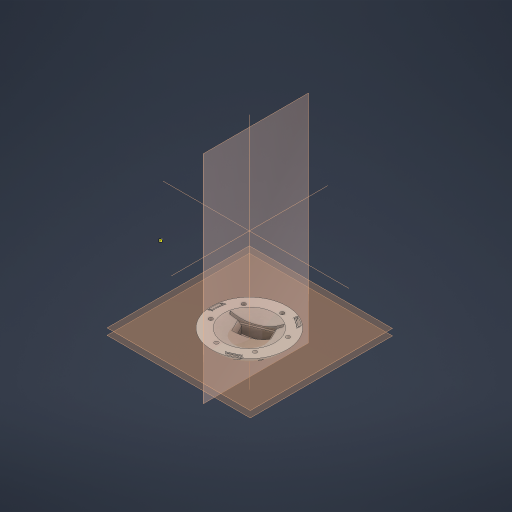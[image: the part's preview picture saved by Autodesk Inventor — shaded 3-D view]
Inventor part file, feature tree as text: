
AUTODESK INVENTOR PART (.ipt)
format: ipt  version: 2023 (Build 270158000, 158)  size: 2,185,728 bytes
history: native  units: mm
features: sketch x16, extrude x10, projected_geometry x7, other x6, plane x5, pattern_circular x4, reference x3, revolve x2, chamfer x2, sweep x1, shell x1
ambient origin geometry x8: Origin, YZ Plane, XZ Plane, XY Plane, X Axis, Y Axis, Z Axis, Center Point
bodies: Solid1 (feature_tree)
feature tree (57):
  revolve  "Revolution1"  [1 undecoded]
  sketch  "3D Sketch1"
  plane  "Work Plane1"
  sweep  "Sweep1"
  pattern_circular  "Circular Pattern1"  Count=3 Angle=360.0deg
  extrude  "Extrusion1"  TaperAngle=0.0deg  [1 undecoded]
  plane  "Work Plane3"
  sketch  "Sketch12"  dims[d16=0.2mm]
  plane  "Work Plane6"
  extrude  "Extrusion6"  Depth=10.0mm
  chamfer  "Chamfer2"  Distance=10.0mm
  pattern_circular  "Circular Pattern4"  [2 undecoded]
  shell  "Shell2"  Thickness=30.0mm
  extrude  "Extrusion8"  Depth=100.0mm
  extrude  "Extrusion2"  Depth=6.0mm
  sketch  "Sketch7"  dims[d13=1.6mm]
  plane  "Work Plane4"
  extrude  "Extrusion3"  Depth=4.0mm TaperAngle=0.0deg
  extrude  "Extrusion4"  Depth=3.5mm TaperAngle=45.0deg
  pattern_circular  "Circular Pattern2"  Count=3 Angle=360.0deg
  extrude  "Extrusion7"  TaperAngle=30.0deg  [1 undecoded]
  pattern_circular  "Circular Pattern5"  [2 undecoded]
  revolve  "Revolution2"  [1 undecoded]
  extrude  "Extrusion9"  Depth=60.0mm TaperAngle=360.0deg
  extrude  "Extrusion12"  TaperAngle=360.0deg  [1 undecoded]
  extrude  "Extrusion13"  Depth=130.0mm
  chamfer  "Chamfer3"  [1 undecoded]
  sketch  "Sketch1"  dims[d0=160.0mm d1=100.0mm]
  other  "Helical Curve2"
  other  "Project to Surface1"
  sketch  "Sketch2"  dims[d2=90.0deg d7=1200.0mm d8=637.649mm d9=252.623mm d10=0.0mm]
  sketch  "Sketch3"  dims[d11=15.0mm]
  plane  "Work Plane2"
  sketch  "Sketch6"  dims[d12=3.0mm]
  sketch  "Sketch8"  dims[d14=1.478932mm]
  sketch  "Sketch9"  dims[d15=0.2mm]
  sketch  "Sketch13"  dims[d17=0.2mm]
  sketch  "Sketch14"  dims[d18=0.0mm d19=0.0mm d20=30.0mm d21=360.0deg]
  reference  "Reference1"
  sketch  "Sketch15"  dims[d23=120.0mm d24=0.0mm d25=0.0mm]
  sketch  "Sketch16"  dims[d26=-130.0mm d27=-10.0mm d29=1.0mm d30=10.0mm d31=0.0mm]
  sketch  "Sketch17"  dims[d32=6.0mm]
  sketch  "Sketch21"  dims[d33=4.0mm d34=0.0mm]
  reference  "Reference5"
  reference  "Reference6"
  sketch  "Sketch22"  dims[d35=4.0mm d36=4.0mm d37=0.0mm d38=30.0mm d39=360.0deg d51=100.0mm d52=6.0mm d53=4.0mm d54=0.0mm d55=3.5mm d56=1.0mm d57=45.0deg d58=30.0mm d59=360.0deg d61=30.0deg d62=6.0mm d63=4.0mm d64=0.0mm d65=60.0mm d66=360.0deg d68=360.0deg d69=130.0mm d70=0.0mm d71=0.0mm d72=130.0mm d73=0.0mm d74=0.0mm d80=12.2mm d81=0.0mm d82=12.0mm d83=0.0mm d84=0.0mm d85=5.0mm d86=2.0mm d87=45.0deg d88=37.0mm]
  projected_geometry  "Projected Loop1"
  projected_geometry  "Project Cut Edges1"
  projected_geometry  "Project Cut Edges2"
  projected_geometry  "Project Cut Edges3"
  projected_geometry  "Project Cut Edges5"
  projected_geometry  "Project Cut Edges6"
  parser-record x1  (decoder bookkeeping rows leaked as tree rows — omitted from the tree; the rows remain in map.json)
  other  "Assembly1.iam"
  other  "lower_centering_ring:1"
  projected_geometry  "Project Cut Edges7"
  other  "deckel:1"
note: 10 required parameter values undecoded (feature->parameter linkage not recoverable at this tier; creation-order binding heuristic only, values carry confidence <= 0.55)
note: 1 file-system path scrubbed to <path> (originals preserved in map.json)